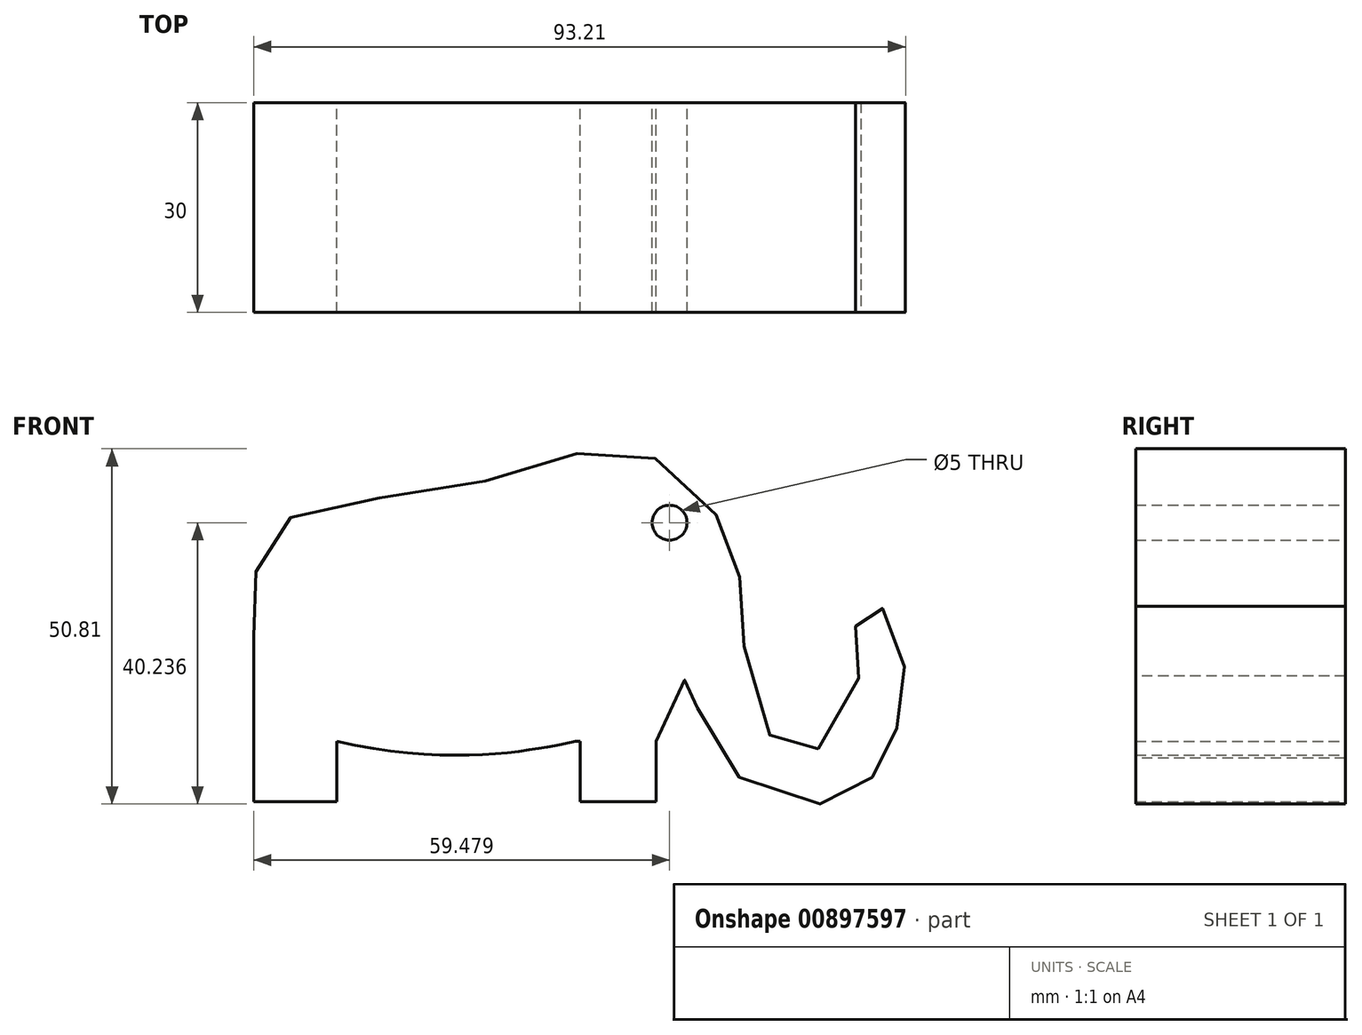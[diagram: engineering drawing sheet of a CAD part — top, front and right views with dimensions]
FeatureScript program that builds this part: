
annotation { "Feature Type Name" : "Feature", "Feature Type Description" : "" }
export const myFeature = defineFeature(function(context is Context, id is Id, definition is map)
    precondition{}
    {
        {
            var Q0;
            Q0=qCreatedBy(makeId("Front.planeOp"),FACE);
            var sketch = newSketch(context, id + "F0", { "sketchPlane" : qUnion([Q0])});
            skLineSegment(sketch, "E0", {"start": v(-30.46, 0) * mm, "end": v(-30.46, 14.6) * mm});
            skLineSegment(sketch, "E1", {"start": v(-30.46, 0) * mm, "end": v(-18.6, 0) * mm});
            skLineSegment(sketch, "E2", {"start": v(-18.6, 8.62) * mm, "end": v(-18.6, 0) * mm});
            skFitSpline(sketch, "E3", {"points": [v(-18.6, 8.62) * mm, v(15.85, 8.62) * mm, v(16.26, 8.62) * mm], "startDerivative": vector(61.85, -14.67) * mm, "endDerivative": vector(2, 0) * mm});
            skLineSegment(sketch, "E4", {"start": v(16.26, 8.62) * mm, "end": v(16.26, 0) * mm});
            skLineSegment(sketch, "E5", {"start": v(16.26, 0) * mm, "end": v(27.1, 0) * mm});
            skLineSegment(sketch, "E6", {"start": v(27.1, 0) * mm, "end": v(27.1, 8.62) * mm});
            skPoint(sketch, "E7.14.internal.snap0", {"position": v(-30.46, 7.3) * mm});
            skFitSpline(sketch, "E7", {"points": [v(-30.46, 14.6) * mm, v(-30.46, 26.67) * mm, v(-27.1, 39.3) * mm, v(0, 45.2) * mm, v(24.57, 49.97) * mm, v(38.04, 36.5) * mm, v(39.45, 23.86) * mm, v(47.03, 6.18) * mm, v(56.3, 18.81) * mm, v(55.73, 25.83) * mm, v(59.1, 27.8) * mm, v(62.75, 16.56) * mm, v(59.94, 7.02) * mm, v(53.48, 0) * mm, v(35.23, 7.3) * mm, v(31.86, 17.97) * mm, v(27.1, 8.62) * mm], "startDerivative": vector(-0.02, 243.27) * mm, "endDerivative": vector(-99.96, -221.26) * mm});
            skSolve(sketch);
        }
        {
            var Q0;
            {var subQ0=sQuery(id+"F0.wireOp",EDGE,"E0");Q0=makeQuery(id+"F0.imprint","IMPRINT",FACE,{"disambiguationData":[TD([[makeQuery(id+"F0.imprint","IMPRINT",EDGE,{"derivedFrom":subQ0}),-1.0]])]});}
            extrude(context, id + "F1", {"entities" : qUnion([Q0]), "depth" : 30 * mm, "offsetDistance" : 25 * mm});
        }
        {
            var Q0;
            Q0=makeQuery(id+"F0.imprint","IMPRINT",FACE,{"disambiguationData":[TD([[makeQuery(id+"F0.imprint","IMPRINT",EDGE,{"derivedFrom":sQuery(id+"F0.wireOp",EDGE,"E0")}),-1.0]])]});
            var sketch = newSketch(context, id + "F2", { "sketchPlane" : qUnion([Q0])});
            skCircle(sketch, "E8", {"center": v(29.02, 39.87) * mm, "radius": 3.2 * mm});
            skSolve(sketch);
        }
        {
            var Q0;
            Q0=sQuery(id+"F2.wireOp",VERTEX,"E8.center");
            var Q1;
            Q1=makeQuery(id+"F1.opExtrude","SWEPT_BODY",BODY,{"disambiguationData":[OSD([sQuery(id+"F0.wireOp",EDGE,"E0"),sQuery(id+"F0.wireOp",EDGE,"E1"),sQuery(id+"F0.wireOp",EDGE,"E2"),sQuery(id+"F0.wireOp",EDGE,"E3"),sQuery(id+"F0.wireOp",EDGE,"E4"),sQuery(id+"F0.wireOp",EDGE,"E5"),sQuery(id+"F0.wireOp",EDGE,"E6"),sQuery(id+"F0.wireOp",EDGE,"E7")])]});
            hole(context, id + "F3", {"style" : HoleStyle.SIMPLE, "endStyle" : HoleEndStyle.THROUGH, "oppositeDirection" : true, "holeDiameter" : 5 * mm, "majorDiameter" : 5 * mm, "isTappedThrough" : true, "tappedDepth" : 12 * mm, "tapClearance" : 3, "locations" : qUnion([Q0]), "scope" : qUnion([Q1])});
        }
    });
